# Revit family: EZO8WSSK
name_source: partatom
category: Plumbing Fixtures
units: mm (PartAtom-declared; Revit-internal decimal feet)

## family parameters
Always vertical = Yes
Cut with Voids When Loaded = Yes
OmniClass Number = 23.45.00.00
OmniClass Title = Sanitary, Laundry, and Cleaning Equipment
Part Type = Normal
Room Calculation Point = No
Round Connector Dimension = Use Diameter
Shared = No
Work Plane-Based = No

## types (2) — shared parameters
Activation by = Electronic Bottle Filler Sensor & Sensor Bubbler
Assembly Code = D2010810
BUBBLER_MATERIAL = Metal - Steel - Stainless - Chrome
Bubbler Style = Flexi-Guard ® Safety Bubbler
CW Connection = Yes
Chilling Capacity = 8.0 GPH
DRAIN_MATERIAL = Metal - Steel - Stainless - Chrome
Description = Elkay EZH2O® Bottle Filling Station with Single ADA Cooler Hands Free Activation Refrigerated Stainless
Dimensions (L x W x H) = 18-3/8 inch x 19- inch x 39 1/16 inch
Drain_Pipe 1 1/4" = 32 mm  [stored 0.104987 ft]
Finish = Stainless Steel
Full Load Amps = 6
HW Connection = No
Inlet_Pipe = 10 mm  [stored 0.0328084 ft]
Installation Location = Indoor
Manufacturer = Elkay
Mounting Type = Wall Mount (On Wall)
No. of Stations Served = 1
Power = 115V/60Hz
Rated Watts = 370
SINK_MATERIAL = Metal - Steel - Stainless - Chrome
Vent Connection = No
Version = 1.0.0.0
Waste Connection = Yes

## per-type parameters (varying)
| type | Approx. Shipping Weight | Special Features |
| EZO8WSSK | 82 lbs | Hands Free, Green Ticker™, Laminar Flow, Antimicrobial, Real Drain |
| LZO8WSSK | 85 lbs | Hands Free, Visual Filter Monitor, Filtered, Green Ticker™, Laminar Flow, Antimicrobial, Real Drain |

note: column(s) folded — value = type name in every type: Model

note: [stored X ft] marks values corroborated as IEEE doubles in the binary element streams (Revit-internal decimal feet)

## geometry (parser evidence)
native form markers: Sweep x20
no freeform markers — native parametric forms only
